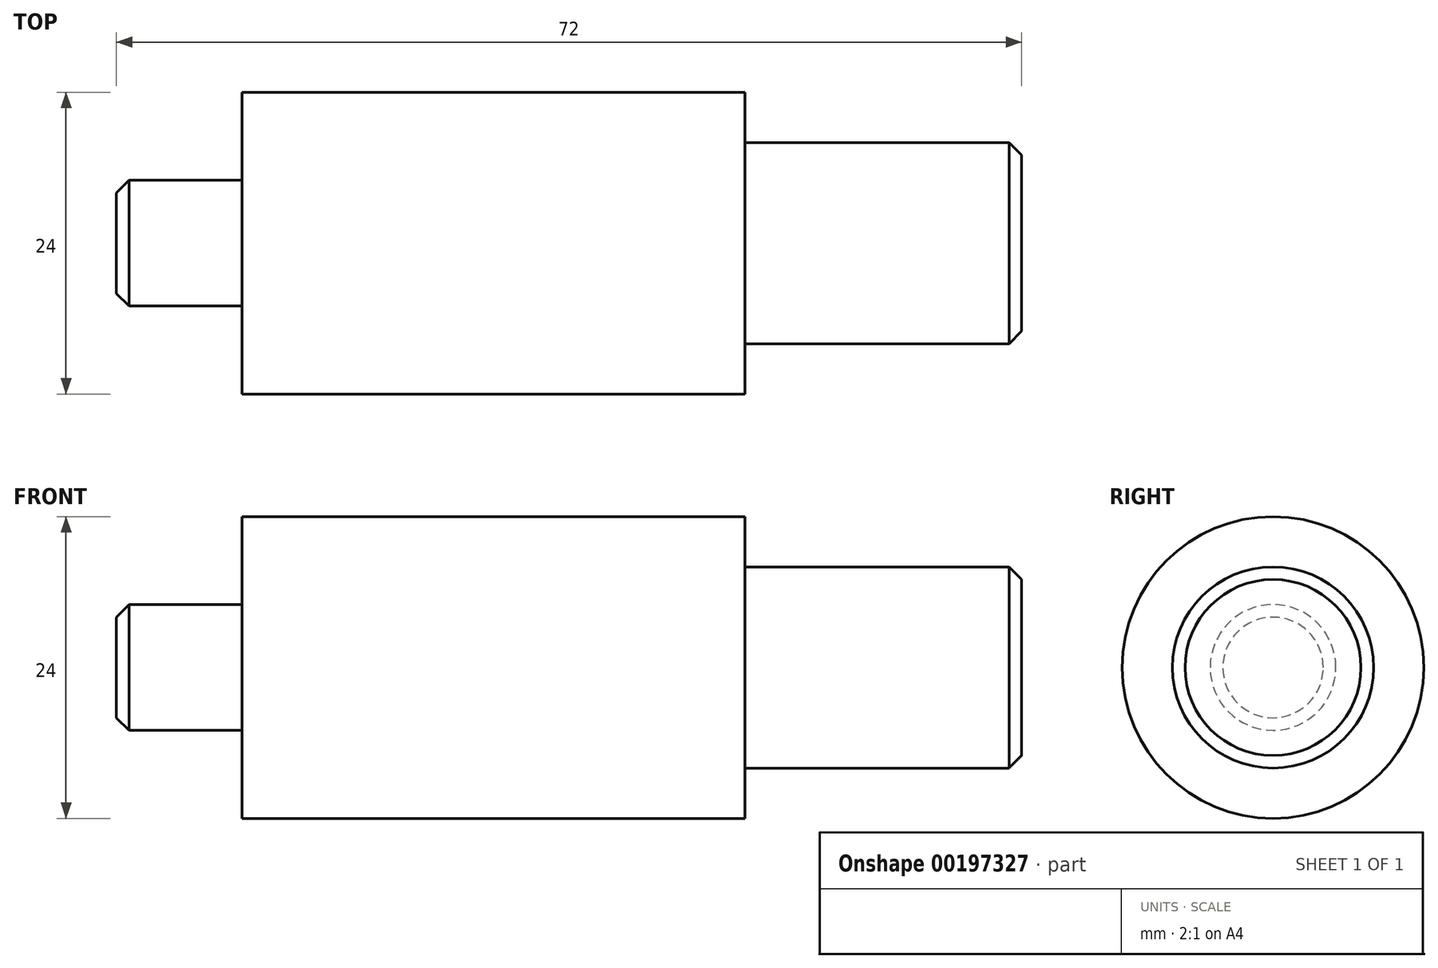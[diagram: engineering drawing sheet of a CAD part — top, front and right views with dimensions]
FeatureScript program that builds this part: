
annotation { "Feature Type Name" : "Feature", "Feature Type Description" : "" }
export const myFeature = defineFeature(function(context is Context, id is Id, definition is map)
    precondition{}
    {
        {
            var Q0;
            Q0=qCreatedBy(makeId("Front.planeOp"),FACE);
            var sketch = newSketch(context, id + "F0", { "sketchPlane" : qUnion([Q0])});
            skLineSegment(sketch, "E0", {"start": v(-4.57, 0) * mm, "end": v(85.66, 0) * mm, "construction": true});
            skLineSegment(sketch, "E1", {"start": v(0, 0) * mm, "end": v(0, 5) * mm});
            skLineSegment(sketch, "E2", {"start": v(0, 5) * mm, "end": v(10, 5) * mm});
            skLineSegment(sketch, "E3", {"start": v(10, 5) * mm, "end": v(10, 12) * mm});
            skLineSegment(sketch, "E4", {"start": v(10, 12) * mm, "end": v(50, 12) * mm});
            skLineSegment(sketch, "E5", {"start": v(50, 12) * mm, "end": v(50, 8) * mm});
            skLineSegment(sketch, "E6", {"start": v(50, 8) * mm, "end": v(72, 8) * mm});
            skLineSegment(sketch, "E7", {"start": v(72, 8) * mm, "end": v(72, 0) * mm});
            skLineSegment(sketch, "E8", {"start": v(72, 0) * mm, "end": v(0, 0) * mm});
            skSolve(sketch);
        }
        {
            var Q0;
            Q0 = qSketchRegion(id + "F0", true);
            var Q1;
            Q1=sQuery(id+"F0.wireOp",EDGE,"E0");
            revolve(context, id + "F1", {"entities" : qUnion([Q0]), "axis" : qUnion([Q1]), "revolveType" : RevolveType.FULL});
        }
        {
            var Q0;
            Q0=makeQuery(id+"F1.opRevolve","SWEPT_EDGE",EDGE,{"disambiguationData":[OSD([sQuery(id+"F0.wireOp",EDGE,"E1"),sQuery(id+"F0.wireOp",EDGE,"E2")])]});
            var Q1;
            Q1=makeQuery(id+"F1.opRevolve","SWEPT_EDGE",EDGE,{"disambiguationData":[OSD([sQuery(id+"F0.wireOp",EDGE,"E6"),sQuery(id+"F0.wireOp",EDGE,"E7")])]});
            chamfer(context, id + "F2", {"entities" : qUnion([Q0, Q1]), "width" : 1 * mm, "tangentPropagation" : true});
        }
    });
